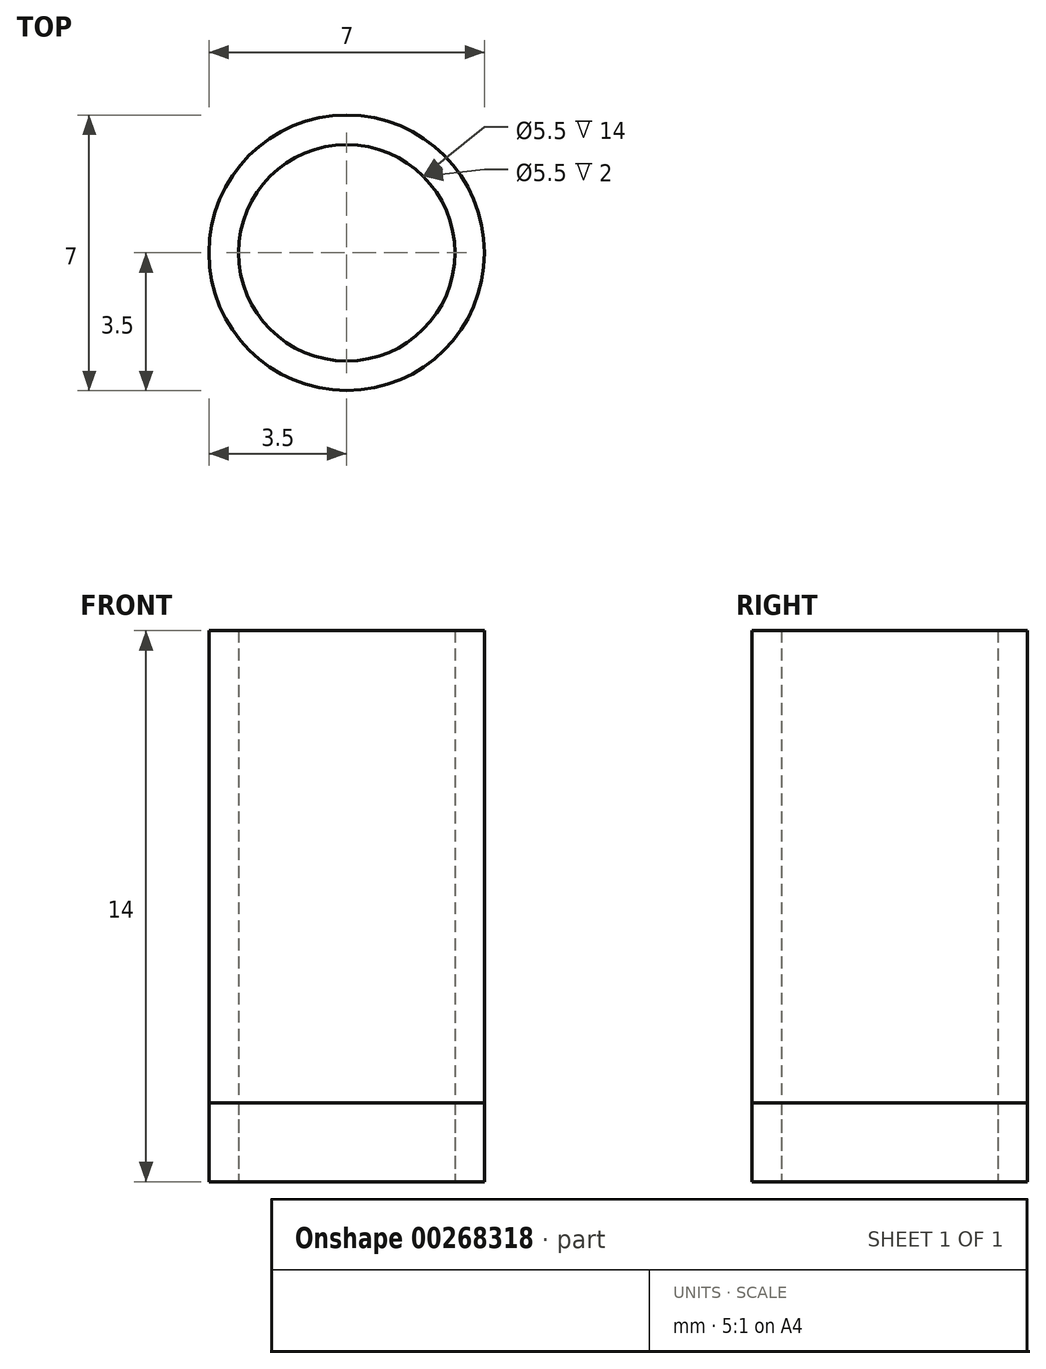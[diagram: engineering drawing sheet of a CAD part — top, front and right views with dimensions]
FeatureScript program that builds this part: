
annotation { "Feature Type Name" : "Feature", "Feature Type Description" : "" }
export const myFeature = defineFeature(function(context is Context, id is Id, definition is map)
    precondition{}
    {
        {
            var Q0;
            Q0=qCreatedBy(makeId("Top.planeOp"),FACE);
            var sketch = newSketch(context, id + "F0", { "sketchPlane" : qUnion([Q0])});
            skCircle(sketch, "E0", {"center": v(0, 0) * mm, "radius": 2.75 * mm});
            skCircle(sketch, "E1", {"center": v(0, 0) * mm, "radius": 3.5 * mm});
            skSolve(sketch);
        }
        {
            var Q0;
            Q0=qSketchRegion(id+"F0",true);
            extrude(context, id + "F1", {"entities" : qUnion([Q0]), "depth" : 2 * mm});
        }
        {
            var Q0;
            Q0=qSketchRegion(id+"F0",true);
            extrude(context, id + "F2", {"entities" : qUnion([Q0]), "depth" : 14 * mm});
        }
    });
